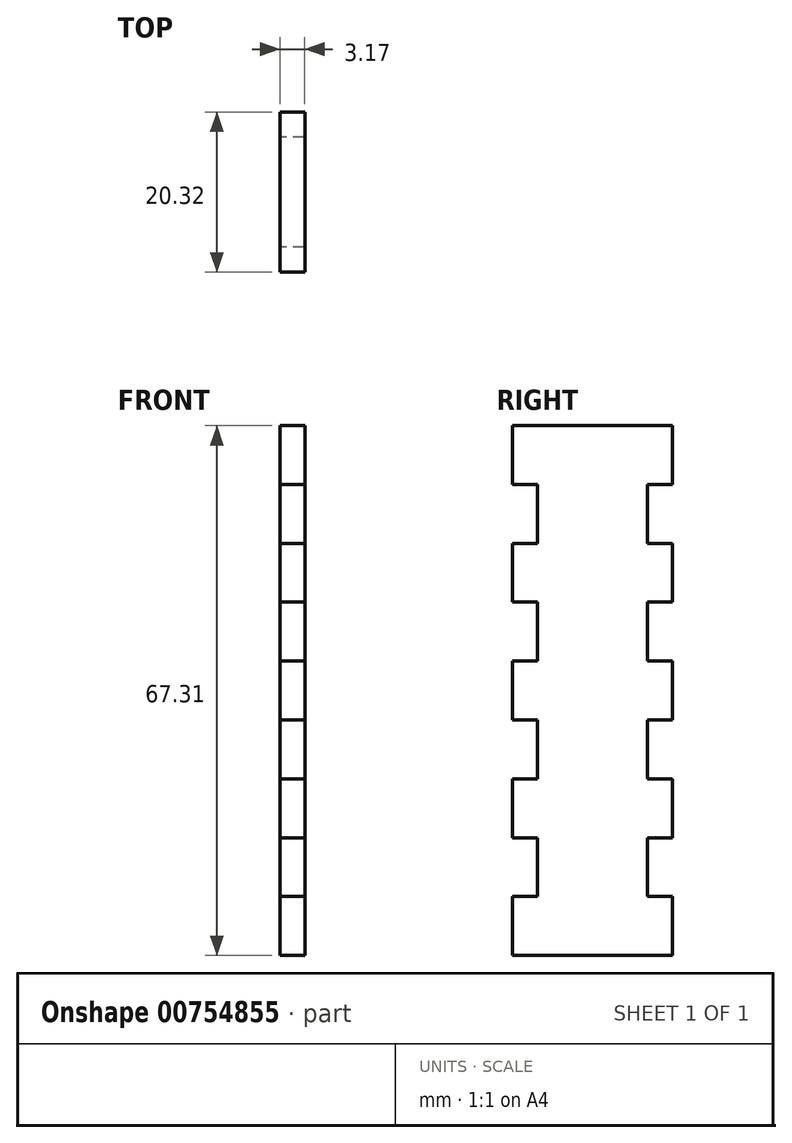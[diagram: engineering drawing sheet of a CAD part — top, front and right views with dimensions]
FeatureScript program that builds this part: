
annotation { "Feature Type Name" : "Feature", "Feature Type Description" : "" }
export const myFeature = defineFeature(function(context is Context, id is Id, definition is map)
    precondition{}
    {
        {
            var Q0;
            Q0=qCreatedBy(makeId("Right.planeOp"),FACE);
            var sketch = newSketch(context, id + "F0", { "sketchPlane" : qUnion([Q0])});
            skLineSegment(sketch, "E0.bottom", {"start": v(-86.36, 59.83) * mm, "end": v(-66.04, 59.83) * mm});
            skLineSegment(sketch, "E0.top", {"start": v(-86.36, -7.48) * mm, "end": v(-66.04, -7.48) * mm});
            skLineSegment(sketch, "E0.left", {"start": v(-86.36, 59.83) * mm, "end": v(-86.36, 52.35) * mm});
            skLineSegment(sketch, "E0.right", {"start": v(-66.04, 59.83) * mm, "end": v(-66.04, 52.35) * mm});
            skLineSegment(sketch, "E1", {"start": v(-83.19, 52.35) * mm, "end": v(-83.19, 44.87) * mm});
            skLineSegment(sketch, "E2", {"start": v(-86.36, 52.35) * mm, "end": v(-83.19, 52.35) * mm});
            skLineSegment(sketch, "E3", {"start": v(-86.36, 44.87) * mm, "end": v(-83.19, 44.87) * mm});
            skLineSegment(sketch, "E4", {"start": v(-86.36, 37.4) * mm, "end": v(-83.19, 37.4) * mm});
            skLineSegment(sketch, "E5", {"start": v(-86.87, 29.92) * mm, "end": v(-83.19, 29.92) * mm});
            skLineSegment(sketch, "E6", {"start": v(-86.36, 22.44) * mm, "end": v(-83.19, 22.44) * mm});
            skLineSegment(sketch, "E7", {"start": v(-86.36, 14.96) * mm, "end": v(-83.19, 14.96) * mm});
            skLineSegment(sketch, "E8", {"start": v(-86.36, 7.48) * mm, "end": v(-83.19, 7.48) * mm});
            skLineSegment(sketch, "E9", {"start": v(-86.36, 0) * mm, "end": v(-83.19, 0) * mm});
            skLineSegment(sketch, "E10.MirrorCS", {"start": v(-69.22, 52.35) * mm, "end": v(-69.22, 44.87) * mm});
            skLineSegment(sketch, "E11", {"start": v(-69.22, 52.35) * mm, "end": v(-66.04, 52.35) * mm});
            skLineSegment(sketch, "E12", {"start": v(-69.22, 44.87) * mm, "end": v(-66.04, 44.87) * mm});
            skLineSegment(sketch, "E13", {"start": v(-69.22, 37.4) * mm, "end": v(-66.04, 37.4) * mm});
            skLineSegment(sketch, "E14", {"start": v(-69.22, 29.92) * mm, "end": v(-66.04, 29.92) * mm});
            skLineSegment(sketch, "E15", {"start": v(-69.22, 22.44) * mm, "end": v(-66.04, 22.44) * mm});
            skLineSegment(sketch, "E16", {"start": v(-69.22, 14.96) * mm, "end": v(-66.04, 14.96) * mm});
            skLineSegment(sketch, "E17", {"start": v(-69.22, 7.48) * mm, "end": v(-66.04, 7.48) * mm});
            skLineSegment(sketch, "E18", {"start": v(-69.22, 0) * mm, "end": v(-66.04, 0) * mm});
            skLineSegment(sketch, "E19.trimOffspring", {"start": v(-86.36, 44.87) * mm, "end": v(-86.36, 37.4) * mm});
            skLineSegment(sketch, "E20.trimOffspring", {"start": v(-86.36, 29.92) * mm, "end": v(-86.36, 22.44) * mm});
            skLineSegment(sketch, "E21.trimOffspring", {"start": v(-86.36, 14.96) * mm, "end": v(-86.36, 7.48) * mm});
            skLineSegment(sketch, "E22.trimOffspring", {"start": v(-86.36, 0) * mm, "end": v(-86.36, -7.48) * mm});
            skLineSegment(sketch, "E23.trimOffspring", {"start": v(-66.04, 0) * mm, "end": v(-66.04, -7.48) * mm});
            skLineSegment(sketch, "E24.trimOffspring", {"start": v(-66.04, 14.96) * mm, "end": v(-66.04, 7.48) * mm});
            skLineSegment(sketch, "E25.trimOffspring", {"start": v(-66.04, 29.92) * mm, "end": v(-66.04, 22.44) * mm});
            skLineSegment(sketch, "E26.trimOffspring", {"start": v(-66.04, 44.87) * mm, "end": v(-66.04, 37.4) * mm});
            skPoint(sketch, "E27.orphan", {"position": v(-83.19, 59.83) * mm});
            skPoint(sketch, "E28.end.orphan", {"position": v(-76.2, -7.48) * mm});
            skPoint(sketch, "E28.start.orphan", {"position": v(-76.2, 59.83) * mm});
            skLineSegment(sketch, "E29.trimOffspring", {"start": v(-69.22, 37.4) * mm, "end": v(-69.22, 29.92) * mm});
            skLineSegment(sketch, "E30.trimOffspring", {"start": v(-69.22, 22.44) * mm, "end": v(-69.22, 14.96) * mm});
            skLineSegment(sketch, "E31.trimOffspring", {"start": v(-69.22, 7.48) * mm, "end": v(-69.22, 0) * mm});
            skPoint(sketch, "E32.orphan", {"position": v(-83.19, -7.48) * mm});
            skLineSegment(sketch, "E33.trimOffspring", {"start": v(-83.19, 7.48) * mm, "end": v(-83.19, 0) * mm});
            skLineSegment(sketch, "E34.trimOffspring", {"start": v(-83.19, 22.44) * mm, "end": v(-83.19, 14.96) * mm});
            skLineSegment(sketch, "E35.trimOffspring", {"start": v(-83.19, 37.4) * mm, "end": v(-83.19, 29.92) * mm});
            skSolve(sketch);
        }
        {
            var Q0;
            Q0=makeQuery(id+"F0.imprint","IMPRINT",FACE,{"disambiguationData":[TD([[makeQuery(id+"F0.imprint","IMPRINT",EDGE,{"derivedFrom":sQuery(id+"F0.wireOp",EDGE,"E0.bottom")}),-1.0]])]});
            extrude(context, id + "F1", {"entities" : qUnion([Q0]), "depth" : 3.17 * mm, "offsetDistance" : 25.4 * mm});
        }
    });
